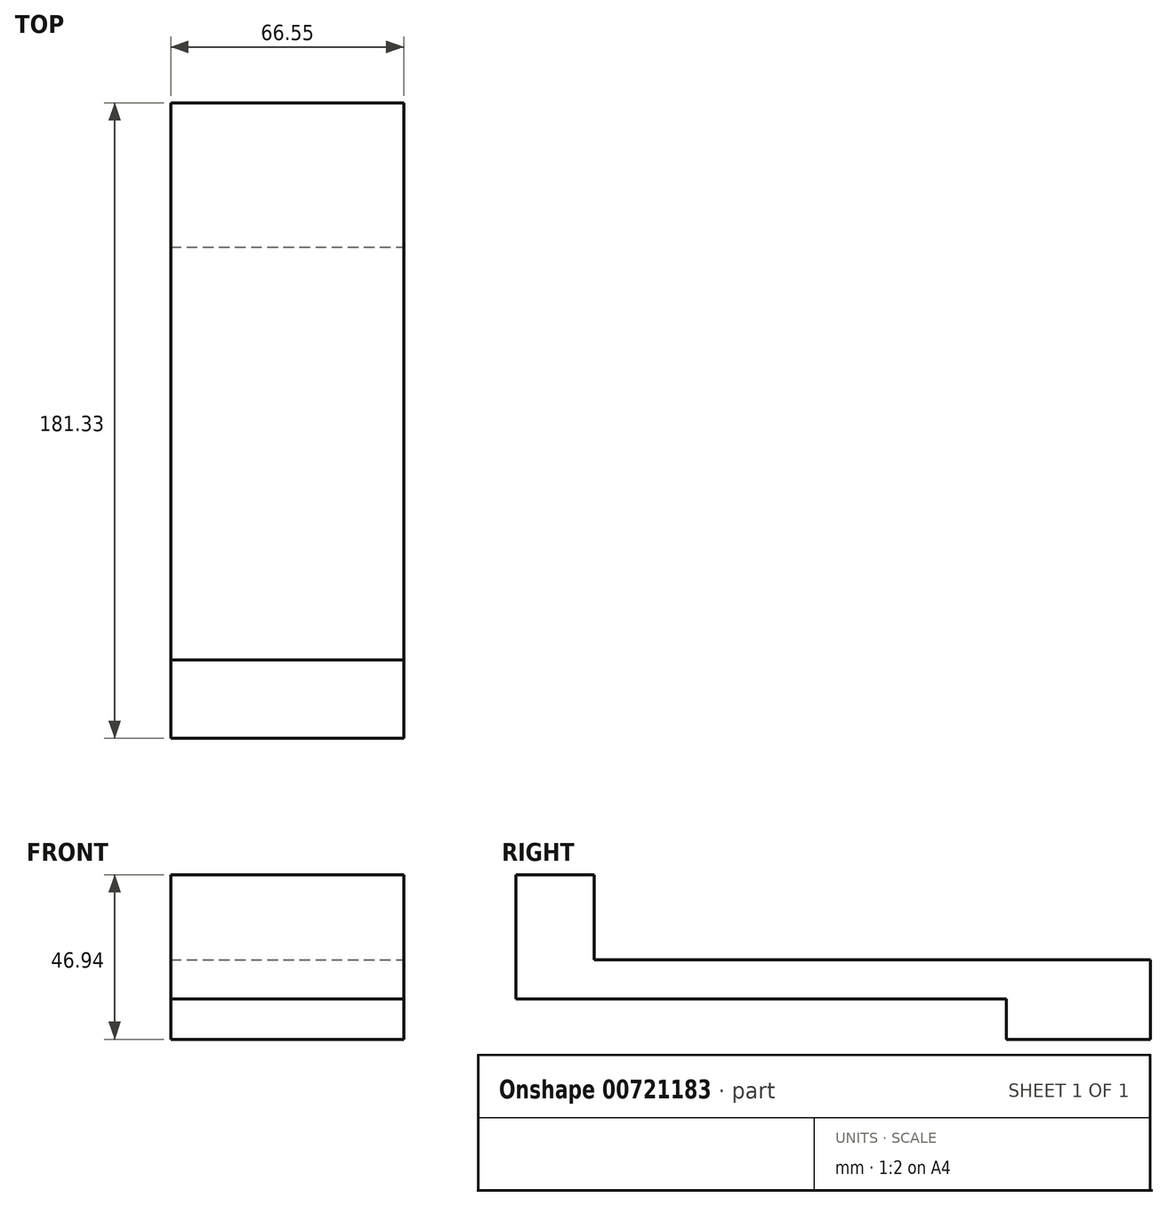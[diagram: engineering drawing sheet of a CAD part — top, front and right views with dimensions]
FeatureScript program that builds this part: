
annotation { "Feature Type Name" : "Feature", "Feature Type Description" : "" }
export const myFeature = defineFeature(function(context is Context, id is Id, definition is map)
    precondition{}
    {
        {
            var Q0;
            Q0=qCreatedBy(makeId("Right.planeOp"),FACE);
            var sketch = newSketch(context, id + "F0", { "sketchPlane" : qUnion([Q0])});
            skLineSegment(sketch, "E0.bottom", {"start": v(58.91, 5.59) * mm, "end": v(-58.91, 5.59) * mm});
            skLineSegment(sketch, "E0.top", {"start": v(58.91, -5.59) * mm, "end": v(-58.91, -5.59) * mm});
            skPoint(sketch, "E0.middle", {"position": v(0, 0) * mm});
            skLineSegment(sketch, "E1.top", {"start": v(-58.91, 29.86) * mm, "end": v(-81.27, 29.86) * mm});
            skLineSegment(sketch, "E1.left", {"start": v(-58.91, 5.59) * mm, "end": v(-58.91, 29.86) * mm});
            skLineSegment(sketch, "E1.right", {"start": v(-81.27, 5.59) * mm, "end": v(-81.27, 29.86) * mm});
            skLineSegment(sketch, "E2.bottom", {"start": v(-58.91, -5.59) * mm, "end": v(-81.27, -5.59) * mm});
            skLineSegment(sketch, "E2.right", {"start": v(-81.27, -5.59) * mm, "end": v(-81.27, 5.59) * mm});
            skLineSegment(sketch, "E3.top", {"start": v(58.91, -17.08) * mm, "end": v(100.06, -17.08) * mm});
            skLineSegment(sketch, "E3.left", {"start": v(58.91, -5.59) * mm, "end": v(58.91, -17.08) * mm});
            skLineSegment(sketch, "E4.bottom", {"start": v(58.91, 5.59) * mm, "end": v(100.06, 5.59) * mm});
            skLineSegment(sketch, "E5", {"start": v(0, 13.07) * mm, "end": v(0, -9.28) * mm});
            skPoint(sketch, "E5.startSnap0", {"position": v(0, 5.59) * mm});
            skLineSegment(sketch, "E6", {"start": v(100.06, 5.59) * mm, "end": v(100.06, -17.08) * mm});
            skSolve(sketch);
        }
        {
            var Q0;
            Q0=makeQuery(id+"F0.imprint","IMPRINT",FACE,{"disambiguationData":[TD([[makeQuery(id+"F0.imprint","IMPRINT",EDGE,{"derivedFrom":sQuery(id+"F0.wireOp",EDGE,"E1.top")}),1.0]])]});
            var Q1;
            Q1=makeQuery(id+"F0.imprint","IMPRINT",FACE,{"disambiguationData":[TD([[makeQuery(id+"F0.imprint","IMPRINT",EDGE,{"derivedFrom":sQuery(id+"F0.wireOp",EDGE,"E3.top")}),1.0]])]});
            extrude(context, id + "F1", {"entities" : qUnion([Q0, Q1]), "oppositeDirection" : true, "depth" : 66.55 * mm, "offsetDistance" : 25.4 * mm});
        }
    });
